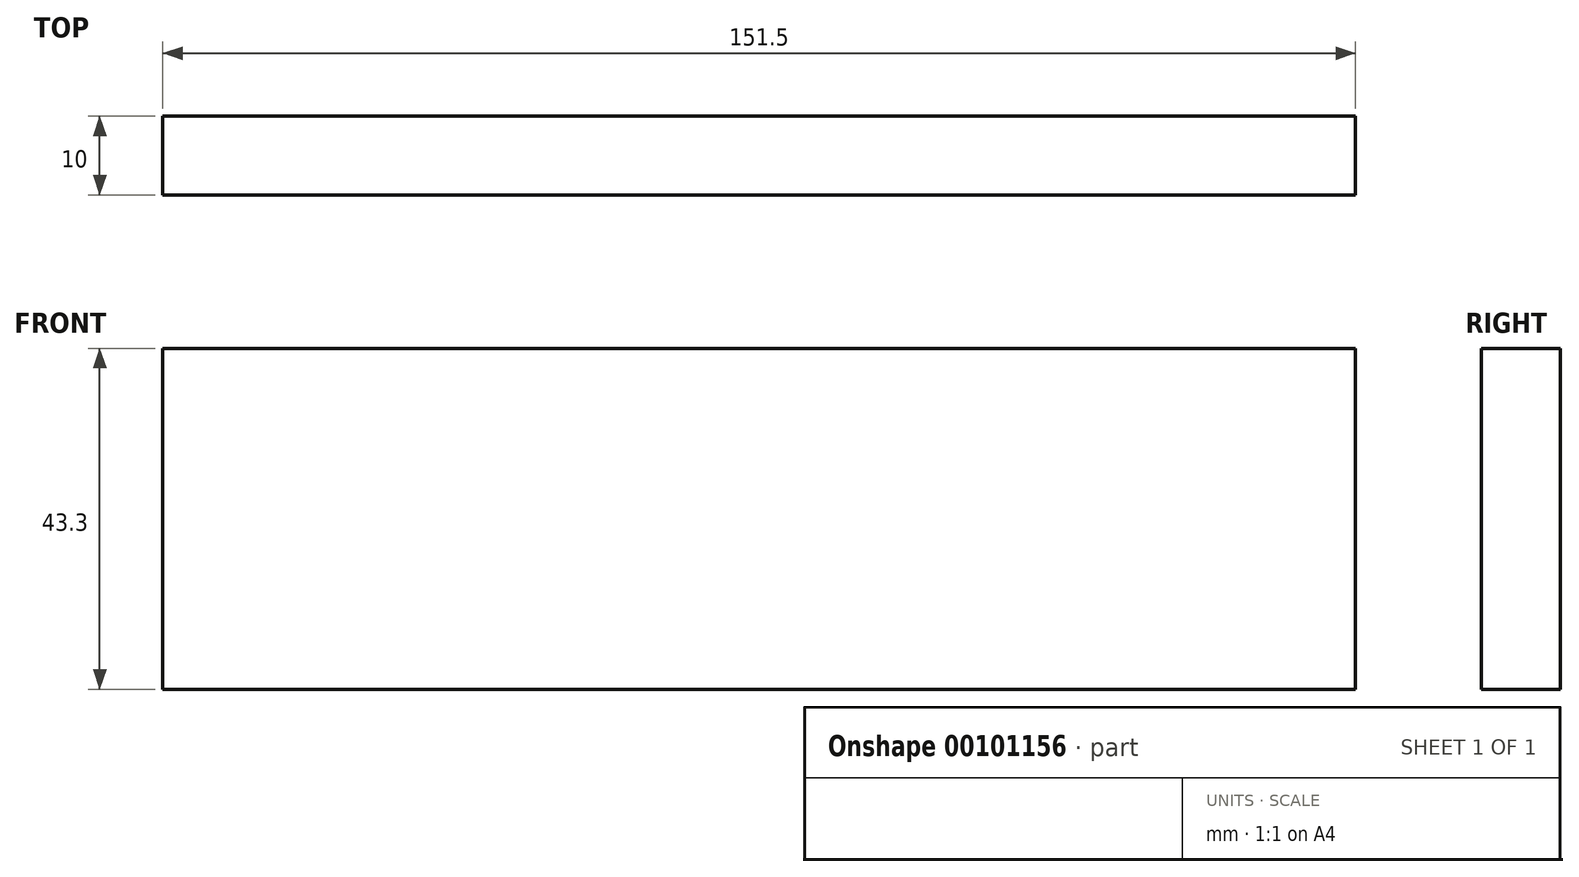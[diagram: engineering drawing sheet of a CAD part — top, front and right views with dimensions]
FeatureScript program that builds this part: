
annotation { "Feature Type Name" : "Feature", "Feature Type Description" : "" }
export const myFeature = defineFeature(function(context is Context, id is Id, definition is map)
    precondition{}
    {
        {
            var Q0;
            Q0=qCreatedBy(makeId("Front.planeOp"),FACE);
            var sketch = newSketch(context, id + "F0", { "sketchPlane" : qUnion([Q0])});
            skLineSegment(sketch, "E0.bottom", {"start": v(75.75, 21.65) * mm, "end": v(-75.75, 21.65) * mm});
            skLineSegment(sketch, "E0.top", {"start": v(75.75, -21.65) * mm, "end": v(-75.75, -21.65) * mm});
            skLineSegment(sketch, "E0.left", {"start": v(75.75, 21.65) * mm, "end": v(75.75, -21.65) * mm});
            skLineSegment(sketch, "E0.right", {"start": v(-75.75, 21.65) * mm, "end": v(-75.75, -21.65) * mm});
            skPoint(sketch, "E0.middle", {"position": v(0, 0) * mm});
            skSolve(sketch);
        }
        {
            var Q0;
            Q0=makeQuery(id+"F0.imprint","IMPRINT",FACE,{"disambiguationData":[TD([[makeQuery(id+"F0.imprint","IMPRINT",EDGE,{"derivedFrom":sQuery(id+"F0.wireOp",EDGE,"E0.bottom")}),1.0]])]});
            extrude(context, id + "F1", {"entities" : qUnion([Q0]), "depth" : 10 * mm});
        }
    });
